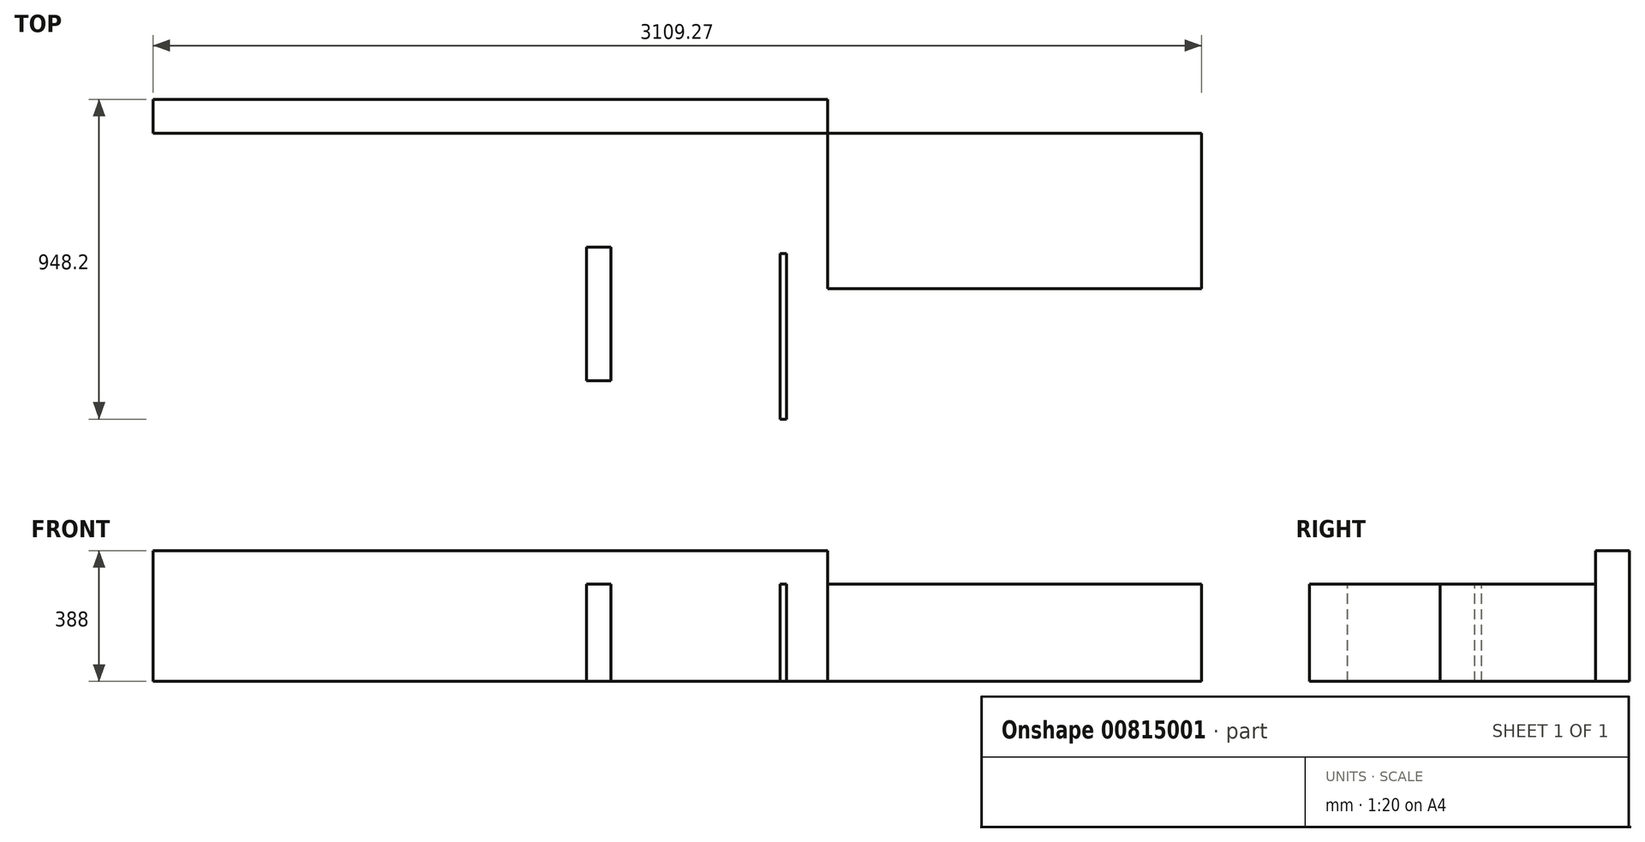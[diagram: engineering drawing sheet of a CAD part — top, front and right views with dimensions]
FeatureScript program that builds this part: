
annotation { "Feature Type Name" : "Feature", "Feature Type Description" : "" }
export const myFeature = defineFeature(function(context is Context, id is Id, definition is map)
    precondition{}
    {
        {
            var Q0;
            Q0=qCreatedBy(makeId("Top.planeOp"),FACE);
            var sketch = newSketch(context, id + "F0", { "sketchPlane" : qUnion([Q0])});
            skLineSegment(sketch, "E0.bottom", {"start": v(-2000, 100) * mm, "end": v(0, 100) * mm});
            skLineSegment(sketch, "E0.top", {"start": v(-2000, 0) * mm, "end": v(0, 0) * mm});
            skLineSegment(sketch, "E0.left", {"start": v(-2000, 100) * mm, "end": v(-2000, 0) * mm});
            skLineSegment(sketch, "E0.right", {"start": v(0, 100) * mm, "end": v(0, 0) * mm});
            skLineSegment(sketch, "E1.bottom", {"start": v(1109.27, 0) * mm, "end": v(0, 0) * mm});
            skLineSegment(sketch, "E1.top", {"start": v(1109.27, -461.54) * mm, "end": v(0, -461.54) * mm});
            skLineSegment(sketch, "E1.left", {"start": v(1109.27, 0) * mm, "end": v(1109.27, -461.54) * mm});
            skLineSegment(sketch, "E1.right", {"start": v(0, 0) * mm, "end": v(0, -461.54) * mm});
            skLineSegment(sketch, "E2.bottom", {"start": v(-714.63, -734.78) * mm, "end": v(-642.47, -734.78) * mm});
            skLineSegment(sketch, "E2.top", {"start": v(-714.63, -337.84) * mm, "end": v(-642.47, -337.84) * mm});
            skLineSegment(sketch, "E2.left", {"start": v(-714.63, -734.78) * mm, "end": v(-714.63, -337.84) * mm});
            skLineSegment(sketch, "E2.right", {"start": v(-642.47, -734.78) * mm, "end": v(-642.47, -337.84) * mm});
            skLineSegment(sketch, "E3.bottom", {"start": v(-121.73, -357.79) * mm, "end": v(-140.5, -357.79) * mm});
            skLineSegment(sketch, "E3.top", {"start": v(-121.73, -848.2) * mm, "end": v(-140.5, -848.2) * mm});
            skLineSegment(sketch, "E3.left", {"start": v(-121.73, -357.79) * mm, "end": v(-121.73, -848.2) * mm});
            skLineSegment(sketch, "E3.right", {"start": v(-140.5, -357.79) * mm, "end": v(-140.5, -848.2) * mm});
            skSolve(sketch);
        }
        {
            var Q0;
            Q0=makeQuery(id+"F0.imprint","IMPRINT",FACE,{"disambiguationData":[TD([[makeQuery(id+"F0.imprint","IMPRINT",EDGE,{"derivedFrom":sQuery(id+"F0.wireOp",EDGE,"E0.bottom")}),-1.0]])]});
            extrude(context, id + "F1", {"entities" : qUnion([Q0]), "depth" : 100 * mm, "offsetDistance" : 25 * mm});
        }
        {
            var Q0;
            Q0 = qSketchRegion(id + "F0", true);
            extrude(context, id + "F2", {"entities" : qUnion([Q0]), "operationType" : NewBodyOperationType.ADD, "oppositeDirection" : true, "depth" : 288 * mm, "offsetDistance" : 25 * mm});
        }
    });
